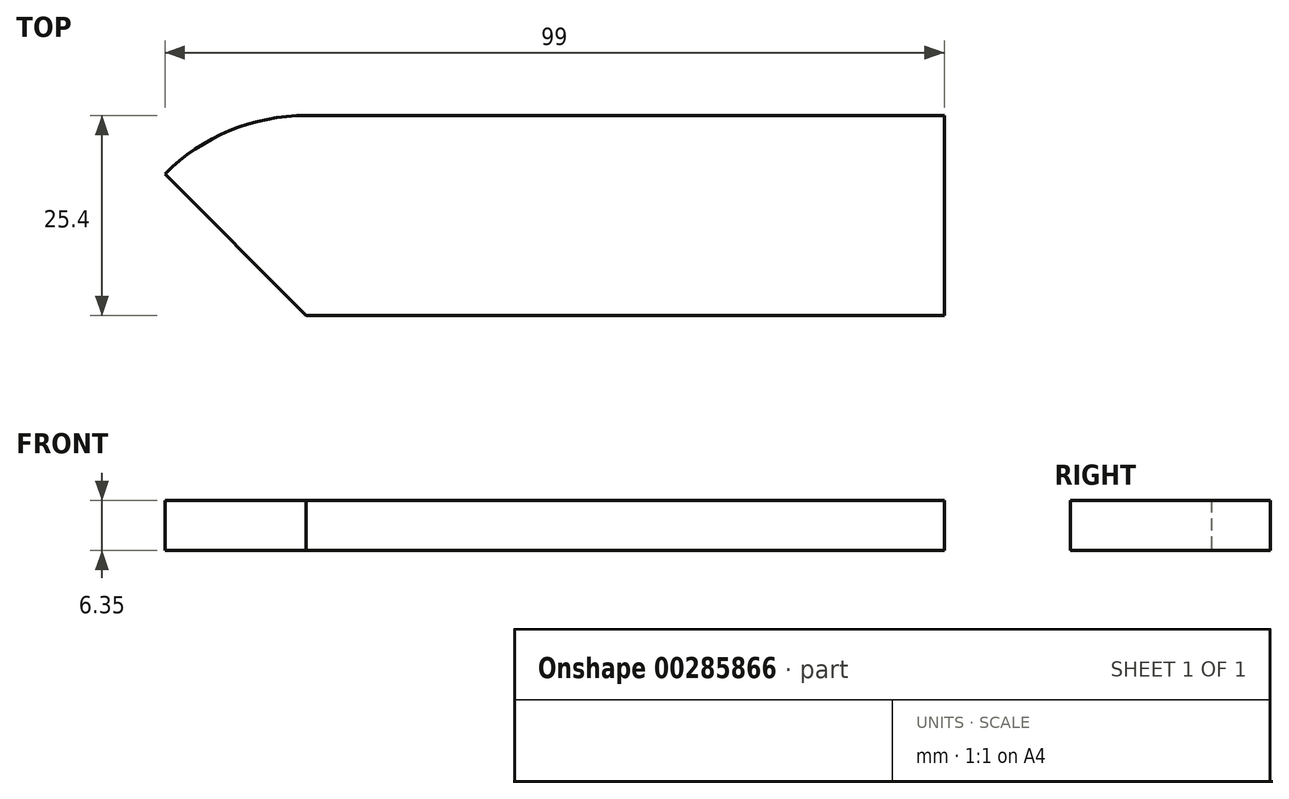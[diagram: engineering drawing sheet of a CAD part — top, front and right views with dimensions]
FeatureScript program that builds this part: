
annotation { "Feature Type Name" : "Feature", "Feature Type Description" : "" }
export const myFeature = defineFeature(function(context is Context, id is Id, definition is map)
    precondition{}
    {
        {
            var Q0;
            Q0=qCreatedBy(makeId("Top.planeOp"),FACE);
            var sketch = newSketch(context, id + "F0", { "sketchPlane" : qUnion([Q0])});
            skLineSegment(sketch, "E0.bottom", {"start": v(0, 0) * mm, "end": v(-81.04, 0) * mm});
            skLineSegment(sketch, "E0.top", {"start": v(0, -25.4) * mm, "end": v(-81.04, -25.4) * mm});
            skLineSegment(sketch, "E0.left", {"start": v(0, 0) * mm, "end": v(0, -25.4) * mm});
            skLineSegment(sketch, "E0.right", {"start": v(-106.44, -25.4) * mm, "end": v(-106.44, -25.4) * mm});
            skPoint(sketch, "E1.visualSharp", {"position": v(-106.44, 0) * mm});
            skArc(sketch, "E1.filletArc", {"start": v(-81.04, 0) * mm, "mid": v(-90.76, -1.93) * mm, "end": v(-99, -7.44) * mm});
            skLineSegment(sketch, "E2", {"start": v(-81.04, -25.4) * mm, "end": v(-99, -7.44) * mm});
            skSolve(sketch);
        }
        {
            var Q0;
            Q0=makeQuery(id+"F0.imprint","IMPRINT",FACE,{"disambiguationData":[TD([[makeQuery(id+"F0.imprint","IMPRINT",EDGE,{"derivedFrom":sQuery(id+"F0.wireOp",EDGE,"E0.bottom")}),1.0]])]});
            extrude(context, id + "F1", {"entities" : qUnion([Q0]), "depth" : 6.35 * mm});
        }
    });
